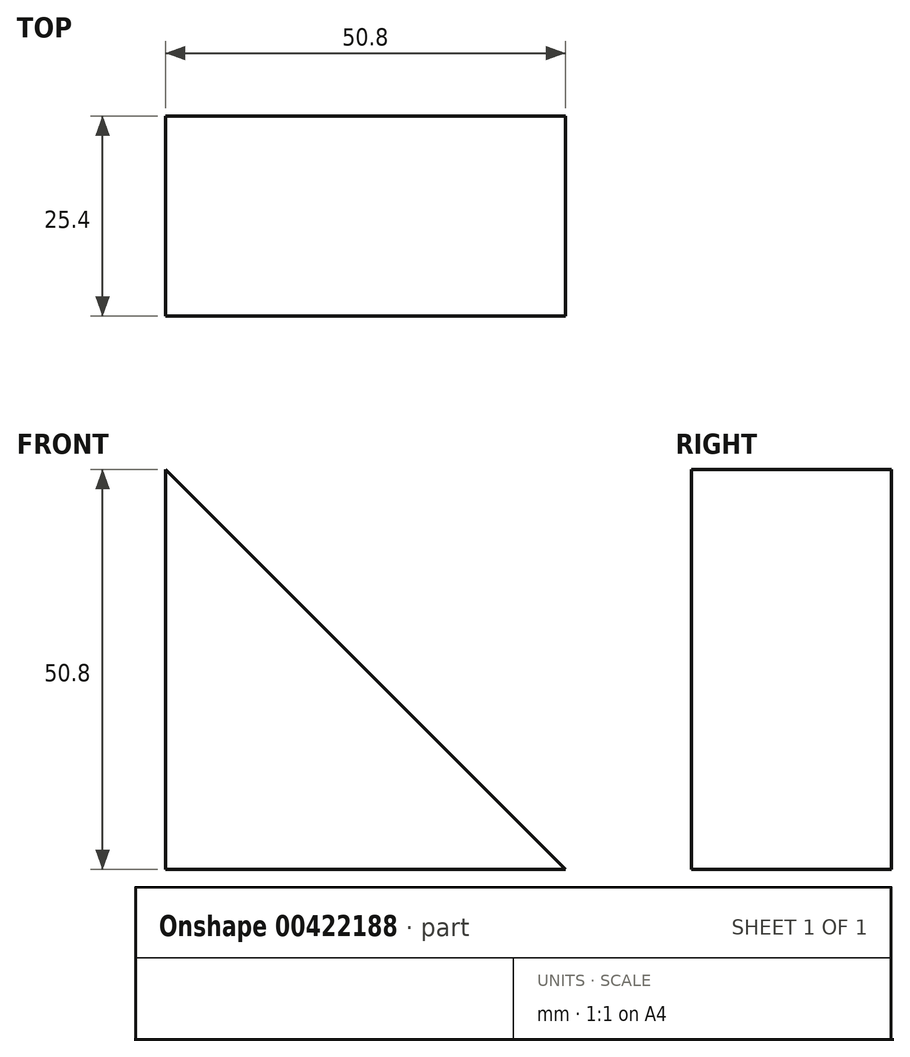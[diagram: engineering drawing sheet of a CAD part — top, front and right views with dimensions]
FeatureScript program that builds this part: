
annotation { "Feature Type Name" : "Feature", "Feature Type Description" : "" }
export const myFeature = defineFeature(function(context is Context, id is Id, definition is map)
    precondition{}
    {
        {
            var Q0;
            Q0=qCreatedBy(makeId("Front.planeOp"),FACE);
            var sketch = newSketch(context, id + "F0", { "sketchPlane" : qUnion([Q0])});
            skLineSegment(sketch, "E0", {"start": v(-28.45, -10.69) * mm, "end": v(-28.45, -61.49) * mm});
            skLineSegment(sketch, "E1", {"start": v(-28.45, -61.49) * mm, "end": v(22.35, -61.49) * mm});
            skLineSegment(sketch, "E2", {"start": v(22.35, -61.49) * mm, "end": v(-28.45, -10.69) * mm});
            skSolve(sketch);
        }
        {
            var Q0;
            Q0=makeQuery(id+"F0.imprint","IMPRINT",FACE,{"disambiguationData":[TD([[makeQuery(id+"F0.imprint","IMPRINT",EDGE,{"derivedFrom":sQuery(id+"F0.wireOp",EDGE,"E0")}),1.0]])]});
            extrude(context, id + "F1", {"entities" : qUnion([Q0]), "depth" : 25.4 * mm});
        }
    });
